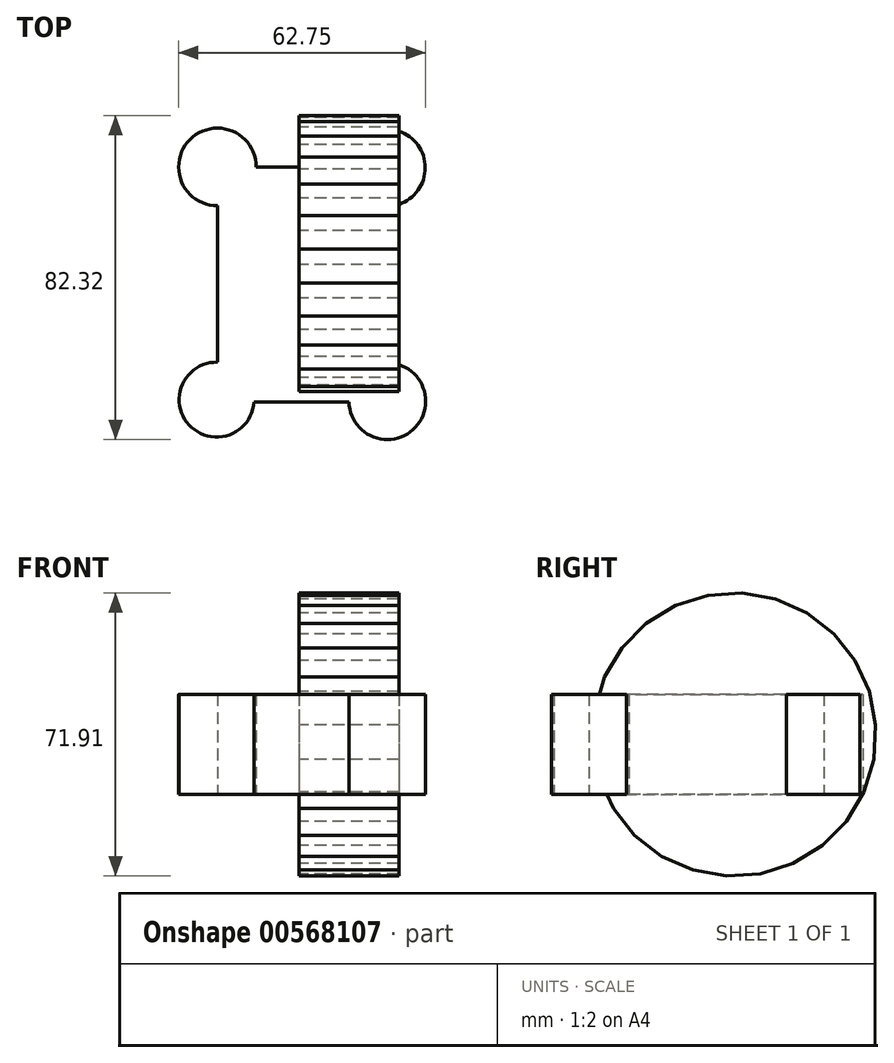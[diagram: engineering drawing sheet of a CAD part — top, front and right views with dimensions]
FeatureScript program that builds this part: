
annotation { "Feature Type Name" : "Feature", "Feature Type Description" : "" }
export const myFeature = defineFeature(function(context is Context, id is Id, definition is map)
    precondition{}
    {
        {
            var Q0;
            Q0=qCreatedBy(makeId("Top.planeOp"),FACE);
            var sketch = newSketch(context, id + "F0", { "sketchPlane" : qUnion([Q0])});
            skLineSegment(sketch, "E0.bottom", {"start": v(-20.7, 22.86) * mm, "end": v(22.27, 22.86) * mm});
            skLineSegment(sketch, "E0.top", {"start": v(-20.7, -36.85) * mm, "end": v(22.27, -36.85) * mm});
            skLineSegment(sketch, "E0.left", {"start": v(-20.7, 22.86) * mm, "end": v(-20.7, -36.85) * mm});
            skLineSegment(sketch, "E0.right", {"start": v(22.27, 22.86) * mm, "end": v(22.27, -36.85) * mm});
            skSolve(sketch);
        }
        {
            var Q0;
            Q0 = qSketchRegion(id + "F0", true);
            extrude(context, id + "F1", {"entities" : qUnion([Q0]), "depth" : 25.4 * mm, "offsetDistance" : 25.4 * mm});
        }
        {
            var Q0;
            Q0=qCreatedBy(makeId("Top.planeOp"),FACE);
            var sketch = newSketch(context, id + "F2", { "sketchPlane" : qUnion([Q0])});
            skCircle(sketch, "E1", {"center": v(22.27, 22.66) * mm, "radius": 9.84 * mm});
            skCircle(sketch, "E2", {"center": v(-20.7, 22.86) * mm, "radius": 9.85 * mm});
            skCircle(sketch, "E3", {"center": v(22.47, -36.65) * mm, "radius": 9.73 * mm});
            skCircle(sketch, "E4", {"center": v(-20.89, -36.26) * mm, "radius": 9.51 * mm});
            skSolve(sketch);
        }
        {
            var Q0;
            Q0 = qSketchRegion(id + "F2", true);
            extrude(context, id + "F3", {"entities" : qUnion([Q0]), "operationType" : NewBodyOperationType.ADD, "depth" : 25.4 * mm, "offsetDistance" : 25.4 * mm});
        }
        {
            var Q0;
            Q0=qCreatedBy(makeId("Right.planeOp"),FACE);
            var sketch = newSketch(context, id + "F4", { "sketchPlane" : qUnion([Q0])});
            skCircle(sketch, "E5.cCircle", {"center": v(0, 15.17) * mm, "radius": 35.75 * mm, "construction": true});
            skLineSegment(sketch, "E5.0", {"start": v(6.7, -20.2) * mm, "end": v(-1.97, -20.78) * mm});
            skLineSegment(sketch, "E5.1", {"start": v(-1.97, -20.78) * mm, "end": v(-10.51, -19.27) * mm});
            skLineSegment(sketch, "E5.2", {"start": v(-10.51, -19.27) * mm, "end": v(-18.45, -15.75) * mm});
            skLineSegment(sketch, "E5.3", {"start": v(-18.45, -15.75) * mm, "end": v(-25.32, -10.44) * mm});
            skLineSegment(sketch, "E5.4", {"start": v(-25.32, -10.44) * mm, "end": v(-30.7, -3.63) * mm});
            skLineSegment(sketch, "E5.5", {"start": v(-30.7, -3.63) * mm, "end": v(-34.32, 4.26) * mm});
            skLineSegment(sketch, "E5.6", {"start": v(-34.32, 4.26) * mm, "end": v(-35.93, 12.8) * mm});
            skLineSegment(sketch, "E5.7", {"start": v(-35.93, 12.8) * mm, "end": v(-35.46, 21.46) * mm});
            skLineSegment(sketch, "E5.8", {"start": v(-35.46, 21.46) * mm, "end": v(-32.92, 29.76) * mm});
            skLineSegment(sketch, "E5.9", {"start": v(-32.92, 29.76) * mm, "end": v(-28.47, 37.22) * mm});
            skLineSegment(sketch, "E5.10", {"start": v(-28.47, 37.22) * mm, "end": v(-22.37, 43.4) * mm});
            skLineSegment(sketch, "E5.11", {"start": v(-22.37, 43.4) * mm, "end": v(-14.97, 47.93) * mm});
            skLineSegment(sketch, "E5.12", {"start": v(-14.97, 47.93) * mm, "end": v(-6.7, 50.56) * mm});
            skLineSegment(sketch, "E5.13", {"start": v(-6.7, 50.56) * mm, "end": v(1.97, 51.13) * mm});
            skLineSegment(sketch, "E5.14", {"start": v(1.97, 51.13) * mm, "end": v(10.51, 49.62) * mm});
            skLineSegment(sketch, "E5.15", {"start": v(10.51, 49.62) * mm, "end": v(18.45, 46.1) * mm});
            skLineSegment(sketch, "E5.16", {"start": v(18.45, 46.1) * mm, "end": v(25.32, 40.78) * mm});
            skLineSegment(sketch, "E5.17", {"start": v(25.32, 40.78) * mm, "end": v(30.7, 33.98) * mm});
            skLineSegment(sketch, "E5.18", {"start": v(30.7, 33.98) * mm, "end": v(34.32, 26.09) * mm});
            skLineSegment(sketch, "E5.19", {"start": v(34.32, 26.09) * mm, "end": v(35.93, 17.56) * mm});
            skLineSegment(sketch, "E5.20", {"start": v(35.93, 17.56) * mm, "end": v(35.46, 8.89) * mm});
            skLineSegment(sketch, "E5.21", {"start": v(35.46, 8.89) * mm, "end": v(32.92, 0.59) * mm});
            skLineSegment(sketch, "E5.22", {"start": v(32.92, 0.59) * mm, "end": v(28.47, -6.87) * mm});
            skLineSegment(sketch, "E5.23", {"start": v(28.47, -6.87) * mm, "end": v(22.37, -13.04) * mm});
            skLineSegment(sketch, "E5.24", {"start": v(22.37, -13.04) * mm, "end": v(14.97, -17.58) * mm});
            skLineSegment(sketch, "E5.25", {"start": v(14.97, -17.58) * mm, "end": v(6.7, -20.2) * mm});
            skPoint(sketch, "E5.0.midPoint", {"position": v(2.36, -20.5) * mm});
            skSolve(sketch);
        }
        {
            var Q0;
            Q0 = qSketchRegion(id + "F4", true);
            extrude(context, id + "F5", {"entities" : qUnion([Q0]), "operationType" : NewBodyOperationType.ADD, "depth" : 25.4 * mm, "offsetDistance" : 25.4 * mm});
        }
    });
